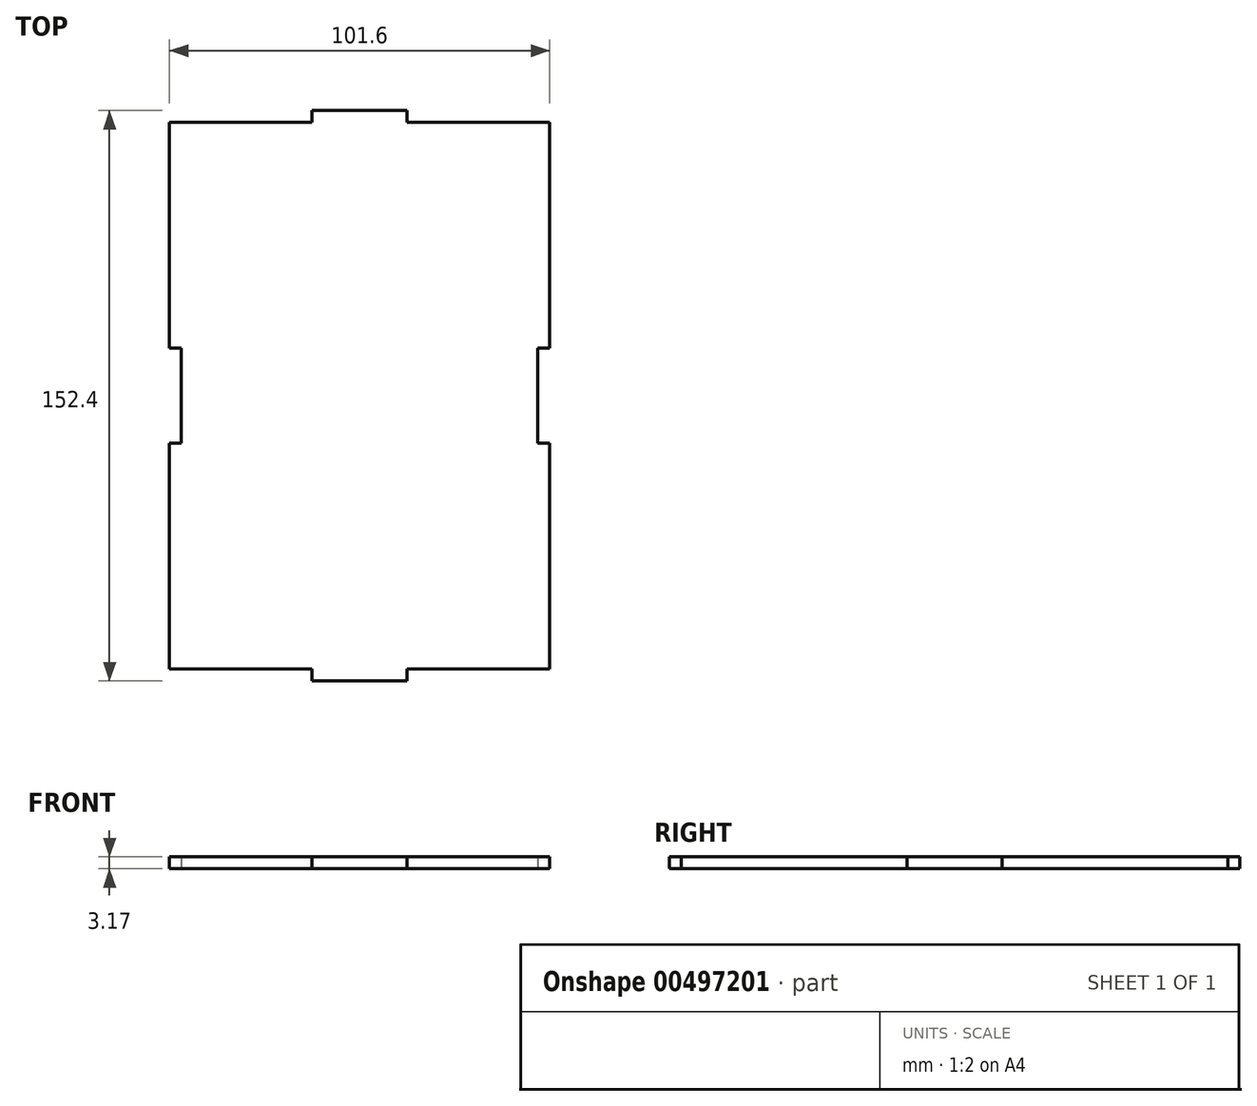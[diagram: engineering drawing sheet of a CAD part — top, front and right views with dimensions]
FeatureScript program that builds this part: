
annotation { "Feature Type Name" : "Feature", "Feature Type Description" : "" }
export const myFeature = defineFeature(function(context is Context, id is Id, definition is map)
    precondition{}
    {
        {
            var Q0;
            Q0=qCreatedBy(makeId("Top.planeOp"),FACE);
            var sketch = newSketch(context, id + "F0", { "sketchPlane" : qUnion([Q0])});
            skLineSegment(sketch, "E0.bottom", {"start": v(50.8, 73.03) * mm, "end": v(-50.8, 73.02) * mm});
            skLineSegment(sketch, "E0.top", {"start": v(50.8, -73.03) * mm, "end": v(-50.8, -73.03) * mm});
            skLineSegment(sketch, "E0.left", {"start": v(50.8, 73.03) * mm, "end": v(50.8, -73.03) * mm});
            skLineSegment(sketch, "E0.right", {"start": v(-50.8, 73.03) * mm, "end": v(-50.8, -73.03) * mm});
            skPoint(sketch, "E0.middle", {"position": v(0, 0) * mm});
            skSolve(sketch);
        }
        {
            var Q0;
            Q0 = qSketchRegion(id + "F0", true);
            extrude(context, id + "F1", {"entities" : qUnion([Q0]), "depth" : 3.17 * mm});
        }
        {
            var Q0;
            Q0=qCreatedBy(makeId("Top.planeOp"),FACE);
            var sketch = newSketch(context, id + "F2", { "sketchPlane" : qUnion([Q0])});
            skLineSegment(sketch, "E1.bottom", {"start": v(-50.8, -12.7) * mm, "end": v(-47.63, -12.7) * mm});
            skLineSegment(sketch, "E1.top", {"start": v(-50.8, 12.7) * mm, "end": v(-47.63, 12.7) * mm});
            skLineSegment(sketch, "E1.left", {"start": v(-50.8, -12.7) * mm, "end": v(-50.8, 12.7) * mm});
            skLineSegment(sketch, "E1.right", {"start": v(-47.63, -12.7) * mm, "end": v(-47.63, 12.7) * mm});
            skLineSegment(sketch, "E2.MirrorCS", {"start": v(50.8, 12.7) * mm, "end": v(47.63, 12.7) * mm});
            skLineSegment(sketch, "E3.MirrorCS", {"start": v(50.8, -12.7) * mm, "end": v(50.8, 12.7) * mm});
            skLineSegment(sketch, "E4.MirrorCS", {"start": v(47.63, -12.7) * mm, "end": v(47.63, 12.7) * mm});
            skLineSegment(sketch, "E5.MirrorCS", {"start": v(50.8, -12.7) * mm, "end": v(47.63, -12.7) * mm});
            skSolve(sketch);
        }
        {
            var Q0;
            Q0 = qSketchRegion(id + "F2", true);
            extrude(context, id + "F3", {"entities" : qUnion([Q0]), "operationType" : NewBodyOperationType.REMOVE, "depth" : 3.17 * mm});
        }
        {
            var Q0;
            Q0=qCreatedBy(makeId("Top.planeOp"),FACE);
            var sketch = newSketch(context, id + "F4", { "sketchPlane" : qUnion([Q0])});
            skLineSegment(sketch, "E6.bottom", {"start": v(-12.7, 73.03) * mm, "end": v(12.7, 73.03) * mm});
            skLineSegment(sketch, "E6.top", {"start": v(-12.7, 76.2) * mm, "end": v(12.7, 76.2) * mm});
            skLineSegment(sketch, "E6.left", {"start": v(-12.7, 73.03) * mm, "end": v(-12.7, 76.2) * mm});
            skLineSegment(sketch, "E6.right", {"start": v(12.7, 73.03) * mm, "end": v(12.7, 76.2) * mm});
            skLineSegment(sketch, "E7.MirrorCS", {"start": v(12.7, -73.03) * mm, "end": v(12.7, -76.2) * mm});
            skLineSegment(sketch, "E8.MirrorCS", {"start": v(-12.7, -73.03) * mm, "end": v(-12.7, -76.2) * mm});
            skLineSegment(sketch, "E9.MirrorCS", {"start": v(-12.7, -73.03) * mm, "end": v(12.7, -73.03) * mm});
            skLineSegment(sketch, "E10.MirrorCS", {"start": v(-12.7, -76.2) * mm, "end": v(12.7, -76.2) * mm});
            skSolve(sketch);
        }
        {
            var Q0;
            Q0 = qSketchRegion(id + "F4", true);
            extrude(context, id + "F5", {"entities" : qUnion([Q0]), "operationType" : NewBodyOperationType.ADD, "depth" : 3.17 * mm});
        }
    });
